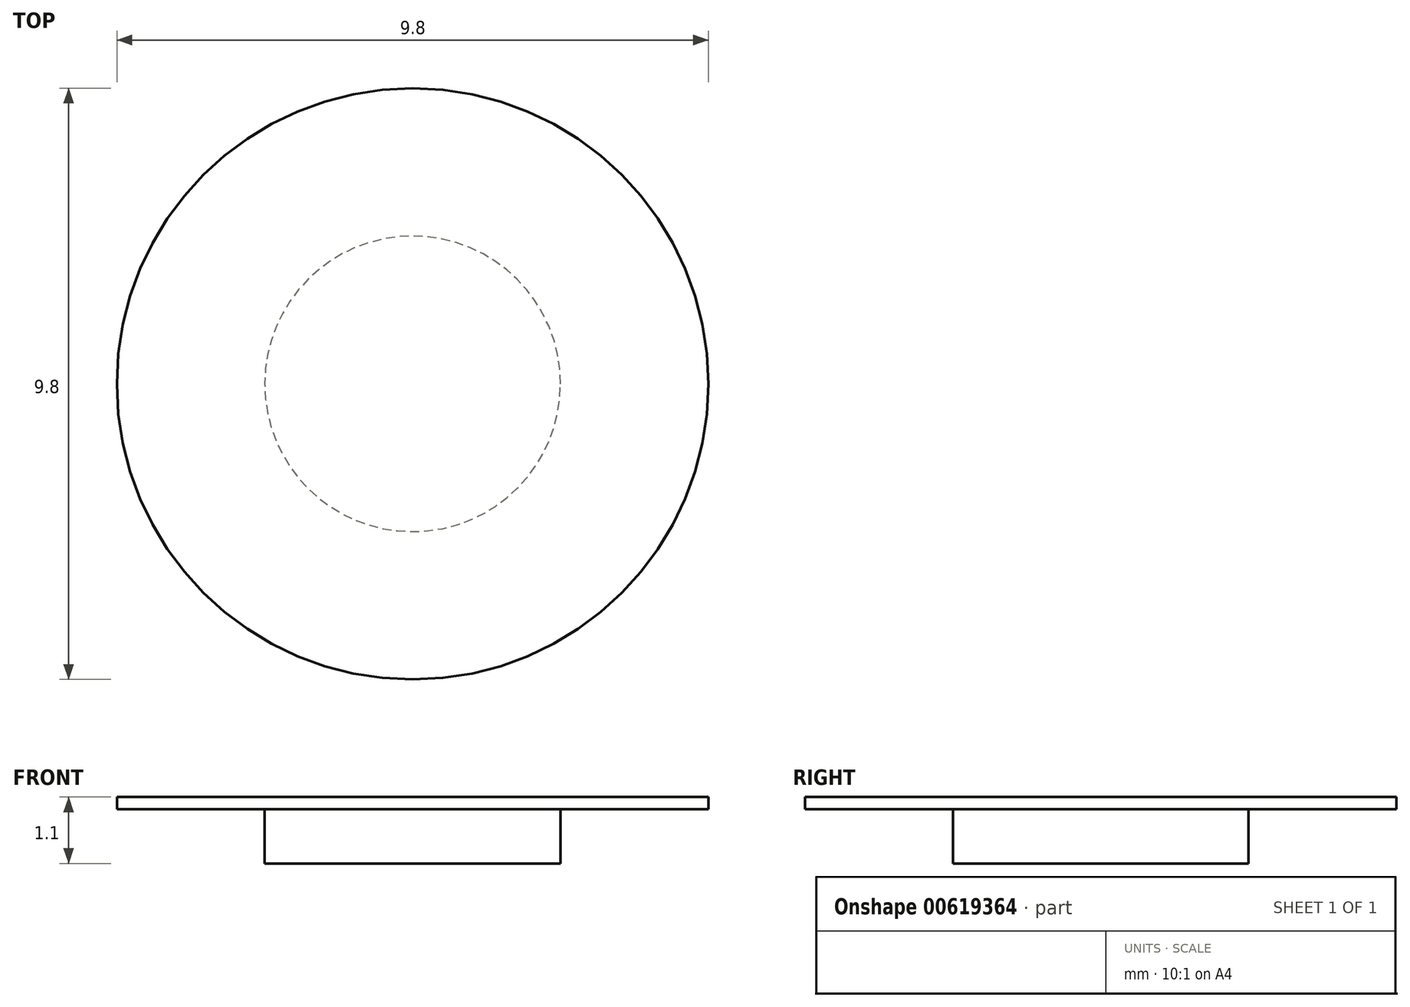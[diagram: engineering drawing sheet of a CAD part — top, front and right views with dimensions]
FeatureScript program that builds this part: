
annotation { "Feature Type Name" : "Feature", "Feature Type Description" : "" }
export const myFeature = defineFeature(function(context is Context, id is Id, definition is map)
    precondition{}
    {
        {
            assignVariable(context, id + "F0", {"name" : "length", "anyValue" : 1 - .1});
        }
        {
            assignVariable(context, id + "F1", {"name" : "holediam", "anyValue" : .5 - .1});
        }
        {
            var Q0;
            Q0=qCreatedBy(makeId("Top.planeOp"),FACE);
            var sketch = newSketch(context, id + "F2", { "sketchPlane" : qUnion([Q0])});
            skCircle(sketch, "E0", {"center": v(0, 0) * mm, "radius": 4.9 * mm});
            skCircle(sketch, "E1", {"center": v(0, 0) * mm, "radius": 2.45 * mm});
            skSolve(sketch);
        }
        {
            var Q0;
            Q0=makeQuery(id+"F2.imprint","IMPRINT",FACE,{"disambiguationData":[TD([[makeQuery(id+"F2.imprint","IMPRINT",EDGE,{"derivedFrom":sQuery(id+"F2.wireOp",EDGE,"E1")}),1.0]])]});
            var Q1;
            Q1=makeQuery(id+"F2.imprint","IMPRINT",FACE,{"disambiguationData":[TD([[makeQuery(id+"F2.imprint","IMPRINT",EDGE,{"derivedFrom":sQuery(id+"F2.wireOp",EDGE,"E0")}),1.0]])]});
            extrude(context, id + "F3", {"entities" : qUnion([Q0, Q1]), "depth" : (getVariable(context, 'holediam') / 2) * mm, "offsetDistance" : 25 * mm});
        }
        {
            var Q0;
            Q0=makeQuery(id+"F2.imprint","IMPRINT",FACE,{"disambiguationData":[TD([[makeQuery(id+"F2.imprint","IMPRINT",EDGE,{"derivedFrom":sQuery(id+"F2.wireOp",EDGE,"E1")}),1.0]])]});
            extrude(context, id + "F4", {"entities" : qUnion([Q0]), "operationType" : NewBodyOperationType.ADD, "oppositeDirection" : true, "depth" : (getVariable(context, 'length')) * mm, "offsetDistance" : 25 * mm});
        }
    });
